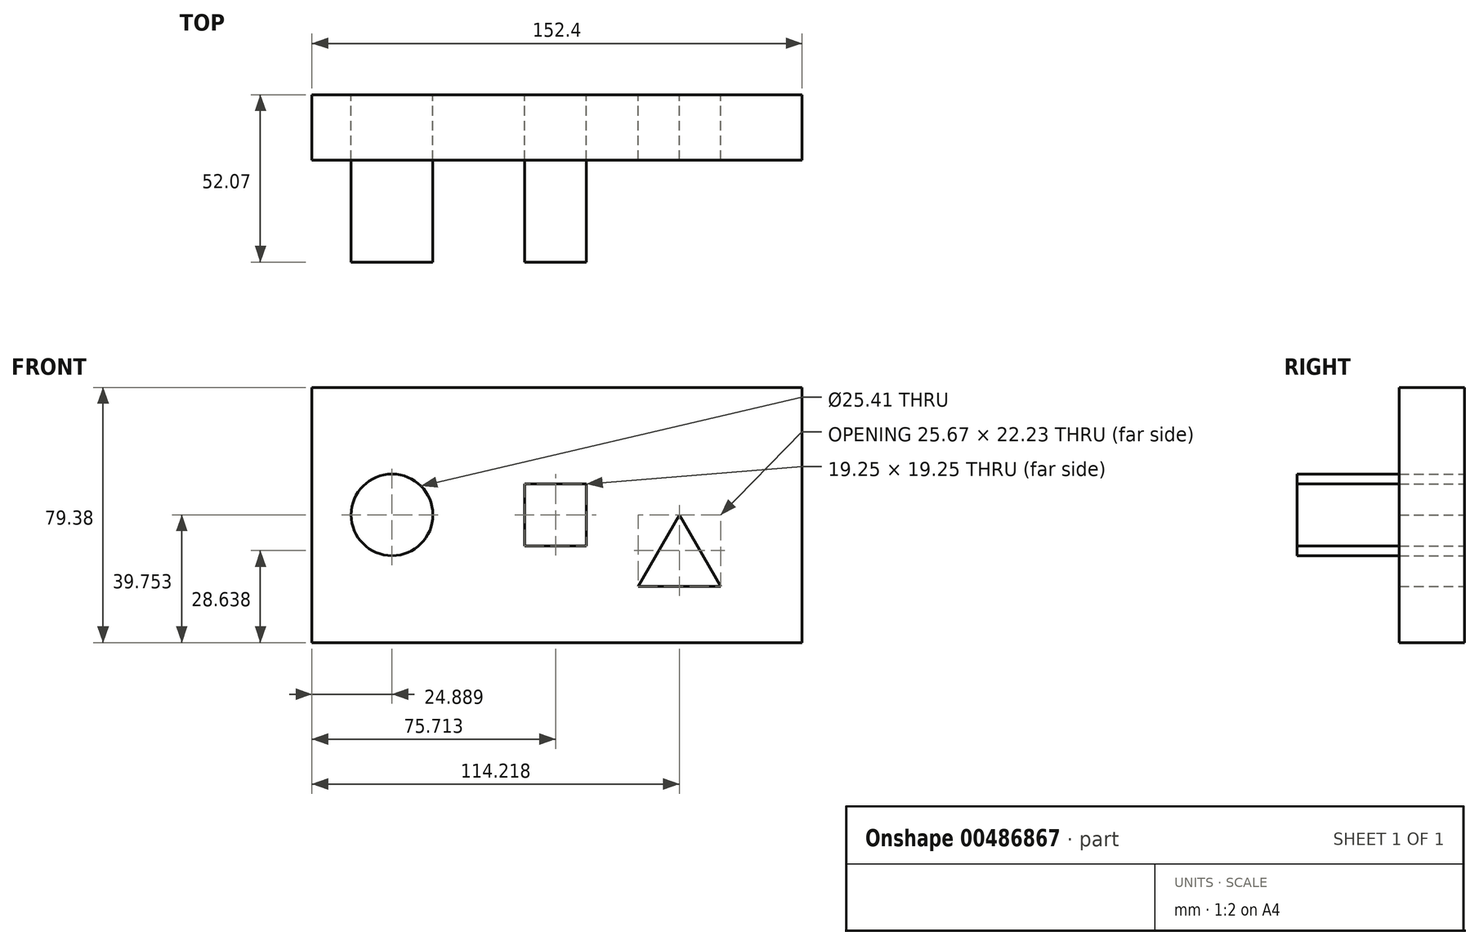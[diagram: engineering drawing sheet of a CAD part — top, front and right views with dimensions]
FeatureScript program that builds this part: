
annotation { "Feature Type Name" : "Feature", "Feature Type Description" : "" }
export const myFeature = defineFeature(function(context is Context, id is Id, definition is map)
    precondition{}
    {
        {
            var Q0;
            Q0=qCreatedBy(makeId("Front.planeOp"),FACE);
            var sketch = newSketch(context, id + "F0", { "sketchPlane" : qUnion([Q0])});
            skLineSegment(sketch, "E0", {"start": v(-30.48, 9.69) * mm, "end": v(-22.14, 9.69) * mm});
            skLineSegment(sketch, "E1.bottom", {"start": v(-22.14, 9.69) * mm, "end": v(-41.4, 9.69) * mm});
            skLineSegment(sketch, "E1.top", {"start": v(-22.14, -9.56) * mm, "end": v(-41.4, -9.56) * mm});
            skLineSegment(sketch, "E1.left", {"start": v(-22.14, 9.69) * mm, "end": v(-22.14, -9.56) * mm});
            skLineSegment(sketch, "E1.right", {"start": v(-41.4, 9.69) * mm, "end": v(-41.4, -9.56) * mm});
            skPoint(sketch, "E1.middle", {"position": v(-31.77, 0.06) * mm});
            skLineSegment(sketch, "E2", {"start": v(6.74, 0.06) * mm, "end": v(19.57, -22.17) * mm});
            skLineSegment(sketch, "E3", {"start": v(19.57, -22.17) * mm, "end": v(-6.1, -22.17) * mm});
            skLineSegment(sketch, "E4", {"start": v(-6.1, -22.17) * mm, "end": v(6.74, 0.06) * mm});
            skCircle(sketch, "E5", {"center": v(-82.6, 0.06) * mm, "radius": 12.7 * mm});
            skLineSegment(sketch, "E6", {"start": v(44.92, 0) * mm, "end": v(44.92, -39.69) * mm});
            skLineSegment(sketch, "E7.bottom", {"start": v(44.92, -39.69) * mm, "end": v(-107.48, -39.69) * mm});
            skLineSegment(sketch, "E7.top", {"start": v(44.92, 39.69) * mm, "end": v(-107.48, 39.69) * mm});
            skLineSegment(sketch, "E7.left", {"start": v(44.92, -39.69) * mm, "end": v(44.92, 39.69) * mm});
            skLineSegment(sketch, "E7.right", {"start": v(-107.48, -39.69) * mm, "end": v(-107.48, 39.69) * mm});
            skSolve(sketch);
        }
        {
            var Q0;
            Q0=makeQuery(id+"F0.imprint","IMPRINT",FACE,{"disambiguationData":[TD([[makeQuery(id+"F0.imprint","IMPRINT",EDGE,{"derivedFrom":sQuery(id+"F0.wireOp",EDGE,"E1.top")}),1.0]])]});
            extrude(context, id + "F1", {"entities" : qUnion([Q0]), "depth" : 20.32 * mm});
        }
        {
            var Q0;
            Q0=makeQuery(id+"F0.imprint","IMPRINT",FACE,{"disambiguationData":[TD([[makeQuery(id+"F0.imprint","IMPRINT",EDGE,{"derivedFrom":sQuery(id+"F0.wireOp",EDGE,"E5")}),1.0]])]});
            extrude(context, id + "F2", {"entities" : qUnion([Q0]), "depth" : 52.07 * mm});
        }
        {
            var Q0;
            Q0=makeQuery(id+"F0.imprint","IMPRINT",FACE,{"disambiguationData":[TD([[makeQuery(id+"F0.imprint","IMPRINT",EDGE,{"derivedFrom":sQuery(id+"F0.wireOp",EDGE,"E1.top")}),-1.0]])]});
            extrude(context, id + "F3", {"entities" : qUnion([Q0]), "depth" : 52.07 * mm, "hasSecondDirection" : true, "secondDirectionOppositeDirection" : true, "secondDirectionDepth" : -20.32 * mm});
        }
    });
